# Revit family: HOSPITAIR G - MVD 26-31 - MVE 38-46 - MVF 55
name_source: partatom
category: Equipement spécialisé
revit_build: Autodesk Revit 2018 (Build: 20170223_1515(x64)
units: mm (PartAtom-declared; Revit-internal decimal feet)

## family parameters
Basée sur le plan de construction = Non
Cote de connecteur circulaire = Utiliser le diamètre
Couper avec des vides une fois chargée = Non
Partagée = Non
Point de calcul de pièce = Non
Toujours verticalement = Oui
Type d'élément = Normal

## types (5) — shared parameters
COS_PHI = 0.9
DOUBLE_ALIMENTATION = Non
Diametre_Connecteur_Alimentation = 58 mm  [stored 0.190289 ft]
Distance_Bord_Pieds = 150 mm
Epaisseur_Porte = 50 mm  [stored 0.164042 ft]
Espacement_Entre_Porte = 5 mm  [stored 0.0164042 ft]
FREQUENCE = 50 Hz
Fabricant = MIL'S
Hauteur_Pieds = 100 mm  [stored 0.328084 ft]
Lien espace client = https://www.mils.fr
NBR_POLES = 3
NEUTRE = Oui
Rayon_Connecteur_Alimentation = 29 mm  [stored 0.0951444 ft]
Rayon_Pieds = 50 mm  [stored 0.164042 ft]
TENSION_ALIM = 400 V
TERRE = Oui
ZONE_MAINTENANCE = Non
Zone_Maintenance_Arriere = 1000 mm
Zone_Maintenance_Avant = 1250 mm
Zone_Maintenance_Droite = 1000 mm
Zone_Maintenance_Gauche = 400 mm  [stored 1.31234 ft]
zero-valued in all types: DIAM_ASPI_AIR

## per-type parameters (varying)
- MVE 38: DESCR_ALIM_X=Alimentation X ; 4G35mm²; DESCR_ASPI=Aspiration Air ; 8336m3/h; DESCR_REFOUL=Refoulement Air ; 336 m3/h ; ID G 1"1/2; DESCR_VENTIL_AIR=Ventilation Air ; 8000 m3/h ; 636 x 350 mm; DIAM_REFOUL_AIR=40 mm  [stored 0.131234 ft]; Debit_aspiration_air=8336.0 m³/h; Debit_refoulement_air=336.0 m³/h; Debit_ventilation_air=8000.0 m³/h; Decalage_Horizontal_Connecteur_Alimentation=250 mm  [stored 0.82021 ft]; Decalage_Horizontal_Connecteur_Refoulement_Air=85 mm  [stored 0.278871 ft]; Decalage_Horizontal_Grille_Ventil=600 mm; Decalage_Vertical_Connecteur_Alimentation=105 mm  [stored 0.344488 ft]; Decalage_Vertical_Connecteur_Refoulement_Air=206 mm  [stored 0.675853 ft]; Decalage_Vertical_Grille_Ventil=388 mm  [stored 1.27297 ft]; Entraxe_Pieds_1=745 mm  [stored 2.44423 ft]; Entraxe_Pieds_2=765 mm  [stored 2.50984 ft]; Entraxe_Pieds_3=975 mm; H1=1690 mm; HAUTEUR=1700 mm; Hauteur_Bouton=1400 mm; Hauteur_Ecran=1500 mm; Hauteur_Totale=1700 mm; LARGEUR=1030 mm; LONGUEUR=1590 mm; Largeur_Porte=640 mm  [stored 2.09974 ft]; Largeur_Porte_Laterale=890 mm; Largeur_Totale=1030 mm; Longueur_Totale=1590 mm; Modèle=HOSPITAIR G - MVE 38; NIVEAU_SONORE(dB(A))=70; POIDS(Kg)=985 mm; PROTEC_ELECT_X=Disjoncteur courbe D - 100 A; PUISS_APPARENTE_X=41111 VA; PUISS_ELECT_X=37 kW; Rayon_Connecteur_Refoulement_Air=20 mm  [stored 0.0656168 ft]; Zone_Maintenance_Hauteur=300 mm
- MVD 26: DESCR_ALIM_X=Alimentation X ; 4G16mm²; DESCR_ASPI=Aspiration Air ;; DESCR_REFOUL=Refoulement Air ; 228 m3/h ; ID G 1"1/4; DESCR_VENTIL_AIR=Ventilation Air ; 4500 m3/h ; 574 x 286 mm; DIAM_REFOUL_AIR=32 mm  [stored 0.104987 ft]; Debit_aspiration_air=4728.0 m³/h; Debit_refoulement_air=228.0 m³/h; Debit_ventilation_air=4500.0 m³/h; Decalage_Horizontal_Connecteur_Alimentation=250 mm  [stored 0.82021 ft]; Decalage_Horizontal_Connecteur_Refoulement_Air=70 mm  [stored 0.229659 ft]; Decalage_Horizontal_Grille_Ventil=533 mm; Decalage_Vertical_Connecteur_Alimentation=100 mm  [stored 0.328084 ft]; Decalage_Vertical_Connecteur_Refoulement_Air=198 mm  [stored 0.649606 ft]; Decalage_Vertical_Grille_Ventil=350 mm  [stored 1.14829 ft]; Entraxe_Pieds_1=662 mm  [stored 2.17192 ft]; Entraxe_Pieds_2=806 mm  [stored 2.64436 ft]; Entraxe_Pieds_3=986 mm; H1=1520 mm; HAUTEUR=1530 mm; Hauteur_Bouton=1230 mm; Hauteur_Ecran=1330 mm; Hauteur_Totale=1530 mm; LARGEUR=900 mm; LONGUEUR=1460 mm; Largeur_Porte=580 mm  [stored 1.90289 ft]; Largeur_Porte_Laterale=750 mm  [stored 2.46063 ft]; Largeur_Totale=900 mm; Longueur_Totale=1460 mm; Modèle=HOSPITAIR G - MVD 26; NIVEAU_SONORE(dB(A))=66; POIDS(Kg)=695 mm  [stored 2.28018 ft]; PROTEC_ELECT_X=Disjoncteur courbe D - 63 A; PUISS_APPARENTE_X=27778 VA; PUISS_ELECT_X=25 kW; Rayon_Connecteur_Refoulement_Air=16 mm  [stored 0.0524934 ft]; Zone_Maintenance_Hauteur=300 mm
- MVD 31: DESCR_ALIM_X=Alimentation X ; 4G25mm²; DESCR_ASPI=Aspiration Air ; 5669 m3/h; DESCR_REFOUL=Refoulement Air ; 269 m3/h ; ID G 1"1/4; DESCR_VENTIL_AIR=Ventilation Air ; 5400 m3/h ; 574 x 286 mm; DIAM_REFOUL_AIR=32 mm  [stored 0.104987 ft]; Debit_aspiration_air=5669.0 m³/h; Debit_refoulement_air=269.0 m³/h; Debit_ventilation_air=5400.0 m³/h; Decalage_Horizontal_Connecteur_Alimentation=250 mm  [stored 0.82021 ft]; Decalage_Horizontal_Connecteur_Refoulement_Air=70 mm  [stored 0.229659 ft]; Decalage_Horizontal_Grille_Ventil=533 mm; Decalage_Vertical_Connecteur_Alimentation=100 mm  [stored 0.328084 ft]; Decalage_Vertical_Connecteur_Refoulement_Air=198 mm  [stored 0.649606 ft]; Decalage_Vertical_Grille_Ventil=350 mm  [stored 1.14829 ft]; Entraxe_Pieds_1=662 mm  [stored 2.17192 ft]; Entraxe_Pieds_2=806 mm  [stored 2.64436 ft]; Entraxe_Pieds_3=986 mm; H1=1520 mm; HAUTEUR=1530 mm; Hauteur_Bouton=1230 mm; Hauteur_Ecran=1330 mm; Hauteur_Totale=1530 mm; LARGEUR=900 mm; LONGUEUR=1460 mm; Largeur_Porte=580 mm  [stored 1.90289 ft]; Largeur_Porte_Laterale=750 mm  [stored 2.46063 ft]; Largeur_Totale=900 mm; Longueur_Totale=1460 mm; Modèle=HOSPITAIR G - MVD 31; NIVEAU_SONORE(dB(A))=69; POIDS(Kg)=750 mm  [stored 2.46063 ft]; PROTEC_ELECT_X=Disjoncteur courbe D - 80 A; PUISS_APPARENTE_X=33333 VA; PUISS_ELECT_X=30 kW; Rayon_Connecteur_Refoulement_Air=16 mm  [stored 0.0524934 ft]; Zone_Maintenance_Hauteur=300 mm
- MVE 46: DESCR_ALIM_X=Alimentation X ; 4G35mm²; DESCR_ASPI=Aspiration Air ; 8411m3/h; DESCR_REFOUL=Refoulement Air ; 411 m3/h ; ID G 1"1/2; DESCR_VENTIL_AIR=Ventilation Air ; 8000 m3/h ; 636 x 350 mm; DIAM_REFOUL_AIR=40 mm  [stored 0.131234 ft]; Debit_aspiration_air=8411.0 m³/h; Debit_refoulement_air=411.0 m³/h; Debit_ventilation_air=8000.0 m³/h; Decalage_Horizontal_Connecteur_Alimentation=250 mm  [stored 0.82021 ft]; Decalage_Horizontal_Connecteur_Refoulement_Air=85 mm  [stored 0.278871 ft]; Decalage_Horizontal_Grille_Ventil=600 mm; Decalage_Vertical_Connecteur_Alimentation=105 mm  [stored 0.344488 ft]; Decalage_Vertical_Connecteur_Refoulement_Air=206 mm  [stored 0.675853 ft]; Decalage_Vertical_Grille_Ventil=388 mm  [stored 1.27297 ft]; Entraxe_Pieds_1=745 mm  [stored 2.44423 ft]; Entraxe_Pieds_2=765 mm  [stored 2.50984 ft]; Entraxe_Pieds_3=975 mm; H1=1690 mm; HAUTEUR=1700 mm; Hauteur_Bouton=1400 mm; Hauteur_Ecran=1500 mm; Hauteur_Totale=1700 mm; LARGEUR=1030 mm; LONGUEUR=1590 mm; Largeur_Porte=640 mm  [stored 2.09974 ft]; Largeur_Porte_Laterale=890 mm; Largeur_Totale=1030 mm; Longueur_Totale=1590 mm; Modèle=HOSPITAIR G - MVE 46; NIVEAU_SONORE(dB(A))=71; POIDS(Kg)=1060 mm; PROTEC_ELECT_X=Disjoncteur courbe D - 100 A; PUISS_APPARENTE_X=50000 VA; PUISS_ELECT_X=45 kW; Rayon_Connecteur_Refoulement_Air=20 mm  [stored 0.0656168 ft]; Zone_Maintenance_Hauteur=300 mm
- MVF 55: DESCR_ALIM_X=Alimentation X ; 4G50mm²; DESCR_ASPI=Aspiration Air ; 9889 m3/h; DESCR_REFOUL=Refoulement Air ; 489 m3/h ; ID G 2"; DESCR_VENTIL_AIR=Ventilation Air ; 9400 m3/h ; 790 x 350 mm; DIAM_REFOUL_AIR=50 mm  [stored 0.164042 ft]; Debit_aspiration_air=9889.0 m³/h; Debit_refoulement_air=489.0 m³/h; Debit_ventilation_air=9400.0 m³/h; Decalage_Horizontal_Connecteur_Alimentation=357 mm  [stored 1.17126 ft]; Decalage_Horizontal_Connecteur_Refoulement_Air=74 mm  [stored 0.242782 ft]; Decalage_Horizontal_Grille_Ventil=546 mm  [stored 1.79134 ft]; Decalage_Vertical_Connecteur_Alimentation=87 mm  [stored 0.285433 ft]; Decalage_Vertical_Connecteur_Refoulement_Air=210 mm  [stored 0.688976 ft]; Decalage_Vertical_Grille_Ventil=446 mm  [stored 1.46325 ft]; Entraxe_Pieds_1=825 mm  [stored 2.70669 ft]; Entraxe_Pieds_2=955 mm; Entraxe_Pieds_3=1165 mm; H1=1855 mm; HAUTEUR=1865 mm; Hauteur_Bouton=1565 mm; Hauteur_Ecran=1665 mm; Hauteur_Totale=1865 mm; LARGEUR=1041 mm; LONGUEUR=1650 mm; Largeur_Porte=670 mm  [stored 2.19816 ft]; Largeur_Porte_Laterale=910 mm; Largeur_Totale=1041 mm; Longueur_Totale=1650 mm; Modèle=HOSPITAIR G - MVF 55; NIVEAU_SONORE(dB(A))=71; POIDS(Kg)=1300 mm; PROTEC_ELECT_X=Disjoncteur courbe D - 125 A; PUISS_APPARENTE_X=61111 VA; PUISS_ELECT_X=55 kW; Rayon_Connecteur_Refoulement_Air=25 mm  [stored 0.082021 ft]; Zone_Maintenance_Hauteur=400 mm  [stored 1.31234 ft]

note: [stored X ft] marks values corroborated as IEEE doubles in the binary element streams (Revit-internal decimal feet)
